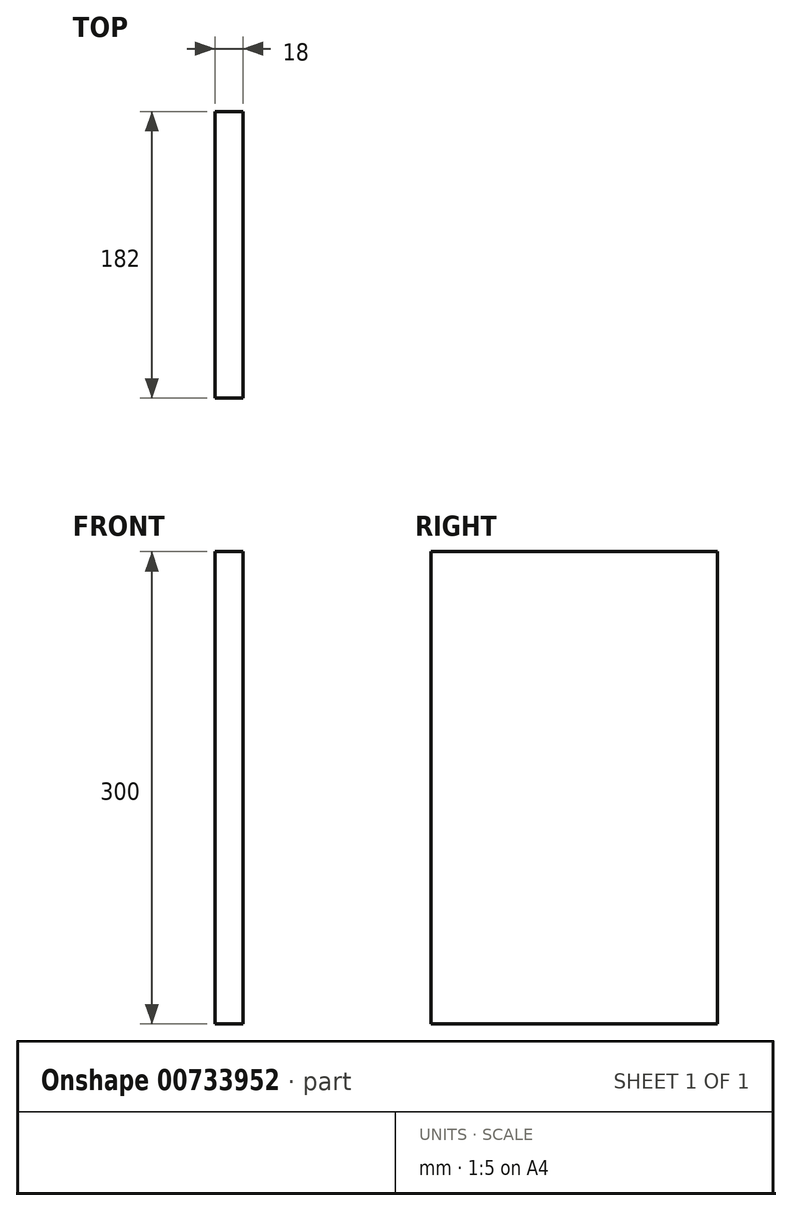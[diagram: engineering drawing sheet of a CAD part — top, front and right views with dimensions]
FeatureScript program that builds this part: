
annotation { "Feature Type Name" : "Feature", "Feature Type Description" : "" }
export const myFeature = defineFeature(function(context is Context, id is Id, definition is map)
    precondition{}
    {
        {
            var Q0;
            Q0=qCreatedBy(makeId("Front.planeOp"),FACE);
            var sketch = newSketch(context, id + "F0", { "sketchPlane" : qUnion([Q0])});
            skLineSegment(sketch, "E0.bottom", {"start": v(0, 0) * mm, "end": v(18, 0) * mm});
            skLineSegment(sketch, "E0.top", {"start": v(0, 300) * mm, "end": v(18, 300) * mm});
            skLineSegment(sketch, "E0.left", {"start": v(0, 0) * mm, "end": v(0, 300) * mm});
            skLineSegment(sketch, "E0.right", {"start": v(18, 0) * mm, "end": v(18, 300) * mm});
            skSolve(sketch);
        }
        {
            var Q0;
            Q0 = qSketchRegion(id + "F0", true);
            extrude(context, id + "F1", {"entities" : qUnion([Q0]), "oppositeDirection" : true, "depth" : 182 * mm, "offsetDistance" : 25 * mm});
        }
    });
